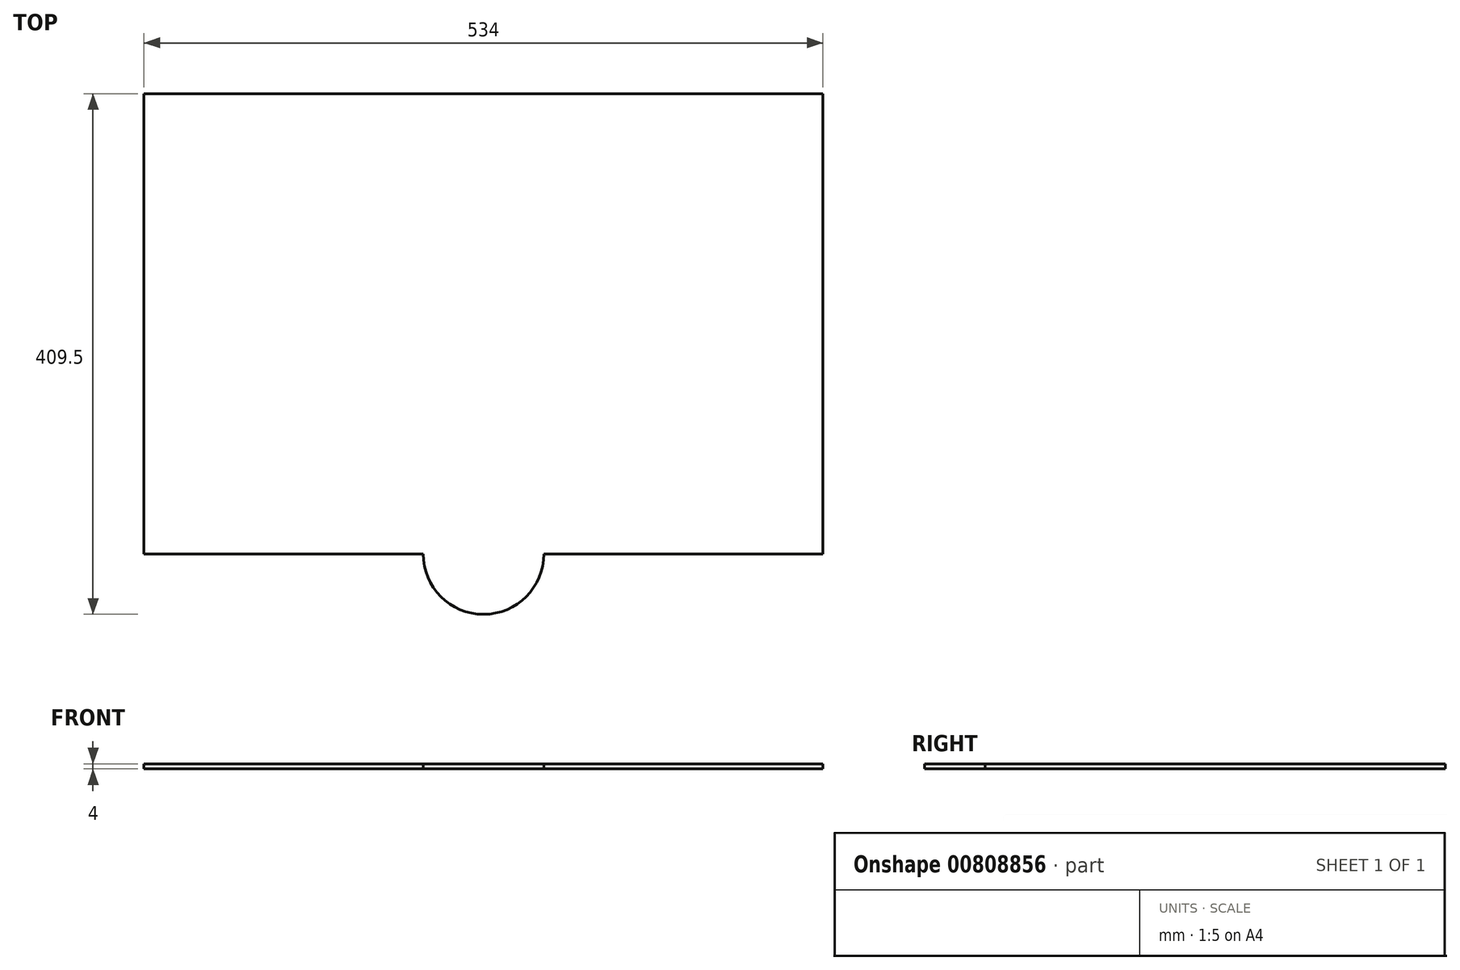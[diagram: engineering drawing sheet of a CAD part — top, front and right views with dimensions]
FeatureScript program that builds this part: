
annotation { "Feature Type Name" : "Feature", "Feature Type Description" : "" }
export const myFeature = defineFeature(function(context is Context, id is Id, definition is map)
    precondition{}
    {
        {
            var Q0;
            Q0=qCreatedBy(makeId("Top.planeOp"),FACE);
            var sketch = newSketch(context, id + "F0", { "sketchPlane" : qUnion([Q0])});
            skLineSegment(sketch, "E0.bottom", {"start": v(0, 0) * mm, "end": v(219.5, 0) * mm});
            skLineSegment(sketch, "E0.top", {"start": v(0, 362) * mm, "end": v(534, 362) * mm});
            skLineSegment(sketch, "E0.left", {"start": v(0, 0) * mm, "end": v(0, 362) * mm});
            skLineSegment(sketch, "E0.right", {"start": v(534, 0) * mm, "end": v(534, 362) * mm});
            skArc(sketch, "E1", {"start": v(219.5, 0) * mm, "mid": v(267, -47.5) * mm, "end": v(314.5, 0) * mm});
            skLineSegment(sketch, "E2.trimOffspring", {"start": v(314.5, 0) * mm, "end": v(534, 0) * mm});
            skSolve(sketch);
        }
        {
            var Q0;
            Q0=makeQuery(id+"F0.imprint","IMPRINT",FACE,{"disambiguationData":[TD([[makeQuery(id+"F0.imprint","IMPRINT",EDGE,{"derivedFrom":sQuery(id+"F0.wireOp",EDGE,"E0.bottom")}),1.0]])]});
            extrude(context, id + "F1", {"entities" : qUnion([Q0]), "depth" : 4 * mm, "offsetDistance" : 25 * mm});
        }
    });
